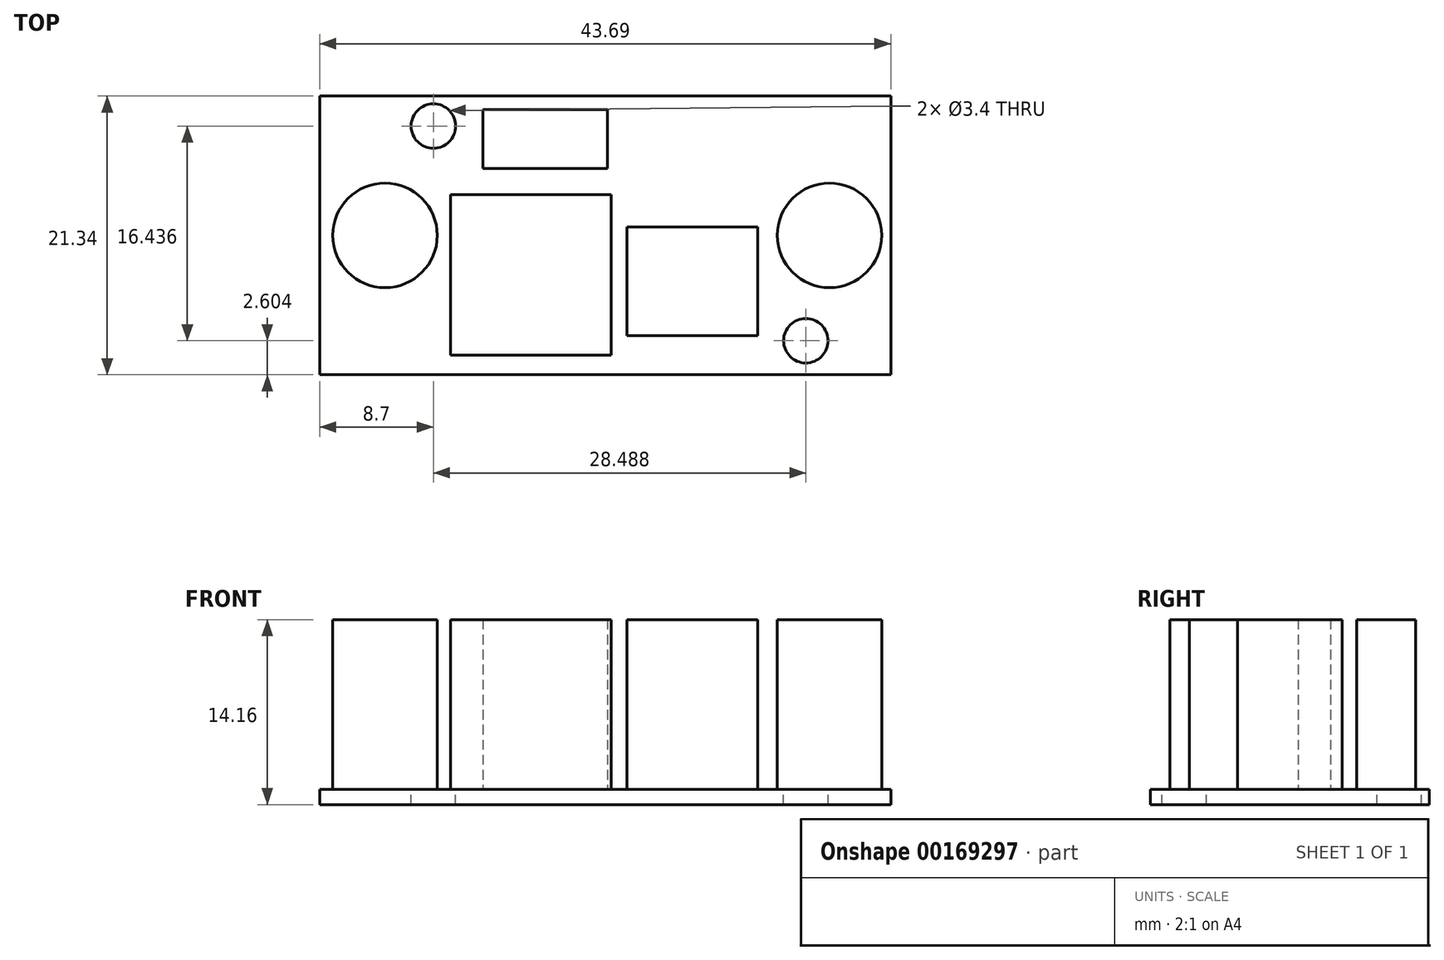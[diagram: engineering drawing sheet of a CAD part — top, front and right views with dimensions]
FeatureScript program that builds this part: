
annotation { "Feature Type Name" : "Feature", "Feature Type Description" : "" }
export const myFeature = defineFeature(function(context is Context, id is Id, definition is map)
    precondition{}
    {
        {
            var Q0;
            Q0=qCreatedBy(makeId("Top.planeOp"),FACE);
            var sketch = newSketch(context, id + "F0", { "sketchPlane" : qUnion([Q0])});
            skLineSegment(sketch, "E0.bottom", {"start": v(0, 0) * mm, "end": v(43.69, 0) * mm});
            skLineSegment(sketch, "E0.top", {"start": v(0, -21.34) * mm, "end": v(43.69, -21.34) * mm});
            skLineSegment(sketch, "E0.left", {"start": v(0, 0) * mm, "end": v(0, -21.34) * mm});
            skLineSegment(sketch, "E0.right", {"start": v(43.69, 0) * mm, "end": v(43.69, -21.34) * mm});
            skSolve(sketch);
        }
        {
            var Q0;
            Q0 = qSketchRegion(id + "F0", true);
            extrude(context, id + "F1", {"entities" : qUnion([Q0]), "depth" : 1.16 * mm});
        }
        {
            var Q0;
            Q0=makeQuery(id+"F1.opExtrude","CAP_FACE",FACE,{"disambiguationData":[OSD([sQuery(id+"F0.wireOp",EDGE,"E0.bottom"),sQuery(id+"F0.wireOp",EDGE,"E0.top"),sQuery(id+"F0.wireOp",EDGE,"E0.left"),sQuery(id+"F0.wireOp",EDGE,"E0.right")])],"isStart":false});
            var sketch = newSketch(context, id + "F2", { "sketchPlane" : qUnion([Q0])});
            skCircle(sketch, "E1", {"center": v(37.19, -18.74) * mm, "radius": 1.7 * mm});
            skCircle(sketch, "E2", {"center": v(8.7, -2.3) * mm, "radius": 1.7 * mm});
            skSolve(sketch);
        }
        {
            var Q0;
            Q0 = qSketchRegion(id + "F2", true);
            extrude(context, id + "F3", {"entities" : qUnion([Q0]), "operationType" : NewBodyOperationType.REMOVE, "oppositeDirection" : true, "depth" : 25 * mm});
        }
        {
            var Q0;
            Q0=makeQuery(id+"F1.opExtrude","CAP_FACE",FACE,{"disambiguationData":[OSD([sQuery(id+"F0.wireOp",EDGE,"E0.bottom"),sQuery(id+"F0.wireOp",EDGE,"E0.top"),sQuery(id+"F0.wireOp",EDGE,"E0.left"),sQuery(id+"F0.wireOp",EDGE,"E0.right")])],"isStart":false});
            var sketch = newSketch(context, id + "F4", { "sketchPlane" : qUnion([Q0])});
            skCircle(sketch, "E3", {"center": v(5, -10.67) * mm, "radius": 4 * mm});
            skCircle(sketch, "E4", {"center": v(39, -10.67) * mm, "radius": 4 * mm});
            skLineSegment(sketch, "E5.bottom", {"start": v(10, -7.54) * mm, "end": v(22.3, -7.54) * mm});
            skLineSegment(sketch, "E5.top", {"start": v(10, -19.84) * mm, "end": v(22.3, -19.84) * mm});
            skLineSegment(sketch, "E5.left", {"start": v(10, -7.54) * mm, "end": v(10, -19.84) * mm});
            skLineSegment(sketch, "E5.right", {"start": v(22.3, -7.54) * mm, "end": v(22.3, -19.84) * mm});
            skLineSegment(sketch, "E6.bottom", {"start": v(23.5, -10.04) * mm, "end": v(33.5, -10.04) * mm});
            skLineSegment(sketch, "E6.top", {"start": v(23.5, -18.34) * mm, "end": v(33.5, -18.34) * mm});
            skLineSegment(sketch, "E6.left", {"start": v(23.5, -10.04) * mm, "end": v(23.5, -18.34) * mm});
            skLineSegment(sketch, "E6.right", {"start": v(33.5, -10.04) * mm, "end": v(33.5, -18.34) * mm});
            skLineSegment(sketch, "E7.bottom", {"start": v(12.5, -1.04) * mm, "end": v(22, -1.04) * mm});
            skLineSegment(sketch, "E7.top", {"start": v(12.5, -5.54) * mm, "end": v(22, -5.54) * mm});
            skLineSegment(sketch, "E7.left", {"start": v(12.5, -1.04) * mm, "end": v(12.5, -5.54) * mm});
            skLineSegment(sketch, "E7.right", {"start": v(22, -1.04) * mm, "end": v(22, -5.54) * mm});
            skPoint(sketch, "E8", {"position": v(0, -10.67) * mm});
            skSolve(sketch);
        }
        {
            var Q0;
            Q0 = qSketchRegion(id + "F4", true);
            extrude(context, id + "F5", {"entities" : qUnion([Q0]), "operationType" : NewBodyOperationType.ADD, "depth" : 13 * mm});
        }
    });
